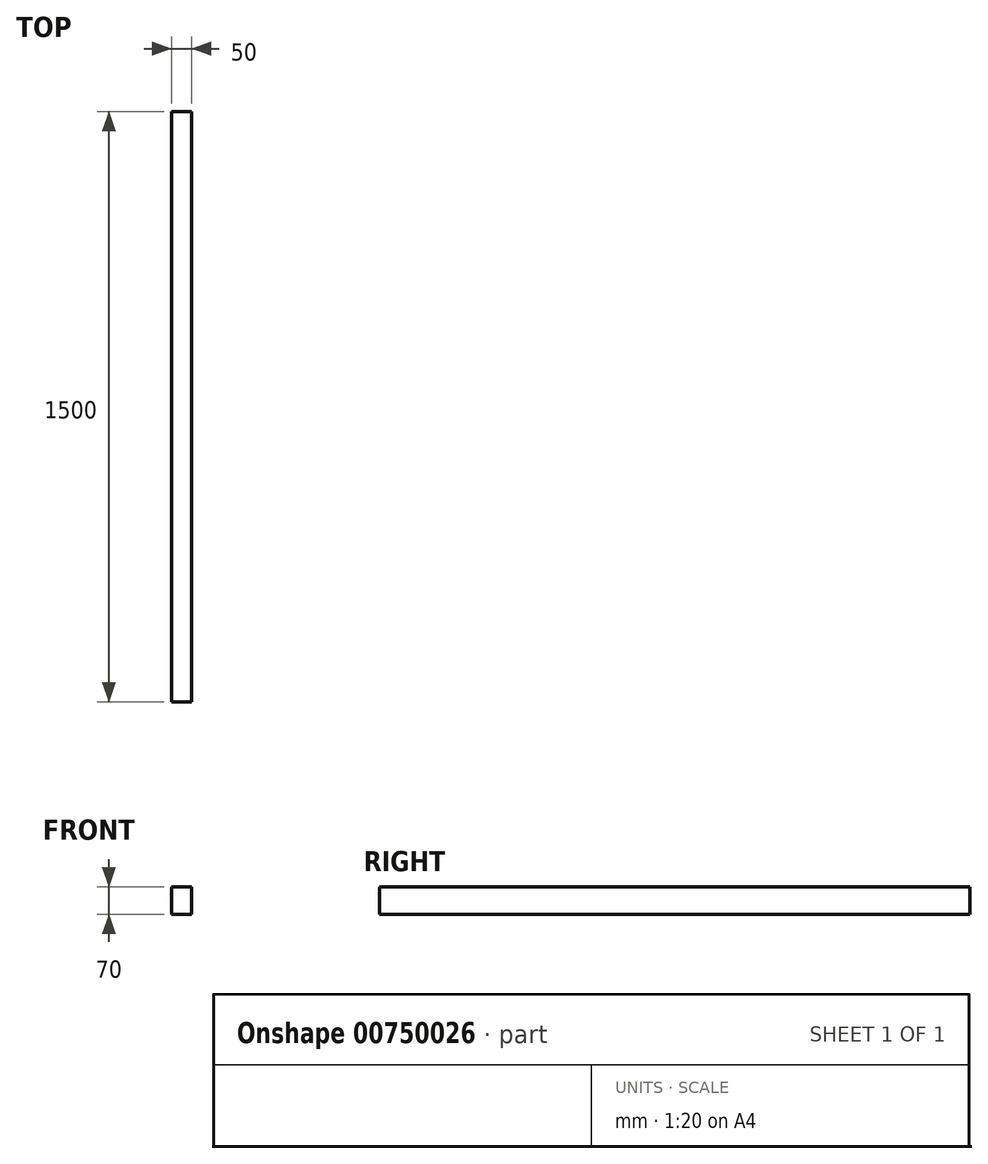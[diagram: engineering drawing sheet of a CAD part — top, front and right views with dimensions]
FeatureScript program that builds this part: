
annotation { "Feature Type Name" : "Feature", "Feature Type Description" : "" }
export const myFeature = defineFeature(function(context is Context, id is Id, definition is map)
    precondition{}
    {
        {
            var Q0;
            Q0=qCreatedBy(makeId("Front.planeOp"),FACE);
            var sketch = newSketch(context, id + "F0", { "sketchPlane" : qUnion([Q0])});
            skLineSegment(sketch, "E0.bottom", {"start": v(0, 0) * mm, "end": v(50, 0) * mm});
            skLineSegment(sketch, "E0.top", {"start": v(0, 70) * mm, "end": v(50, 70) * mm});
            skLineSegment(sketch, "E0.left", {"start": v(0, 0) * mm, "end": v(0, 70) * mm});
            skLineSegment(sketch, "E0.right", {"start": v(50, 0) * mm, "end": v(50, 70) * mm});
            skSolve(sketch);
        }
        {
            var Q0;
            Q0 = qSketchRegion(id + "F0", true);
            extrude(context, id + "F1", {"entities" : qUnion([Q0]), "depth" : 1500 * mm, "offsetDistance" : 25 * mm});
        }
    });
